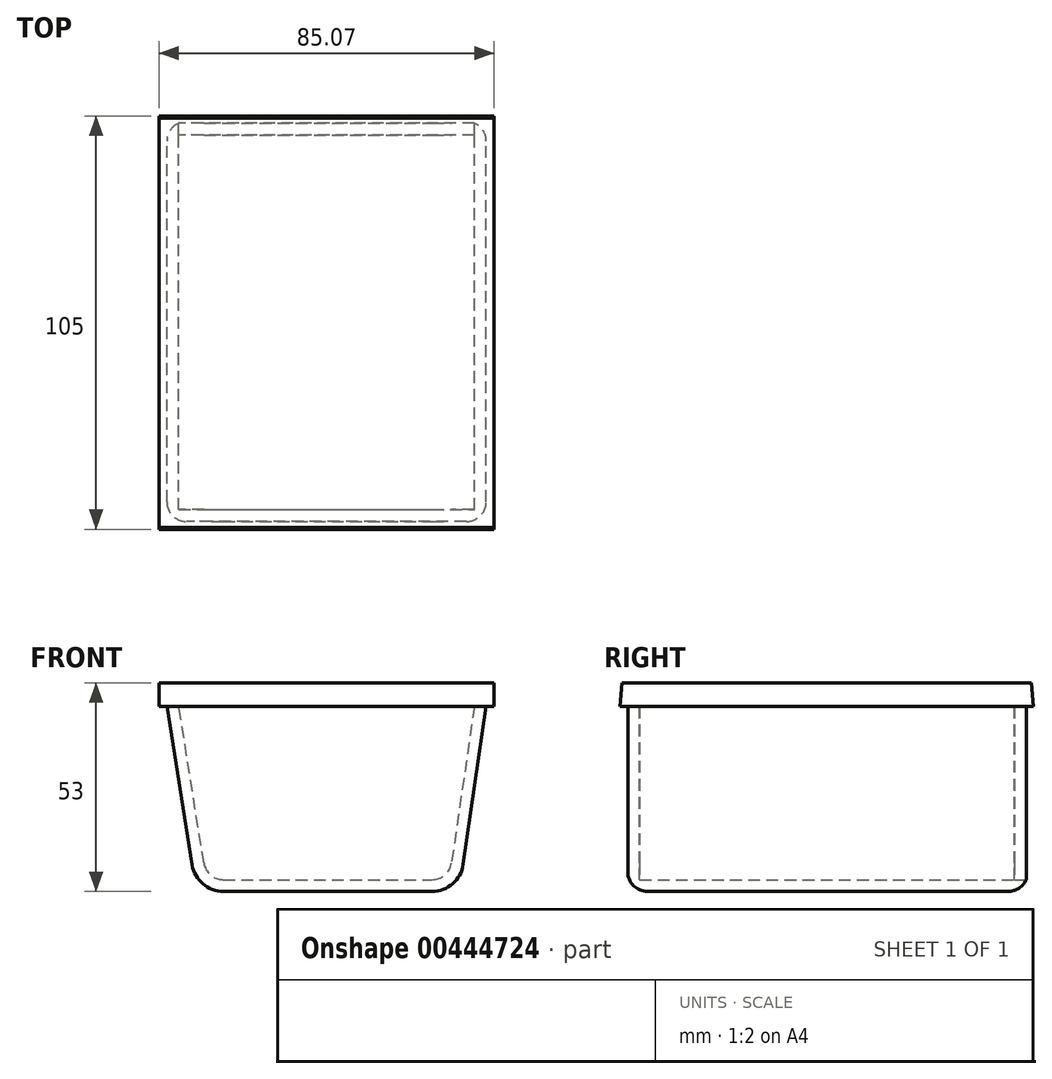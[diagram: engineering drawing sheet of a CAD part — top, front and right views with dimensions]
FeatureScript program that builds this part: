
annotation { "Feature Type Name" : "Feature", "Feature Type Description" : "" }
export const myFeature = defineFeature(function(context is Context, id is Id, definition is map)
    precondition{}
    {
        {
            var Q0;
            Q0=qCreatedBy(makeId("Front.planeOp"),FACE);
            var sketch = newSketch(context, id + "F0", { "sketchPlane" : qUnion([Q0])});
            skLineSegment(sketch, "E0", {"start": v(4.26, 0) * mm, "end": v(57.3, 0) * mm});
            skLineSegment(sketch, "E1", {"start": v(-0.67, 4.21) * mm, "end": v(-7.04, 44) * mm});
            skLineSegment(sketch, "E2", {"start": v(68.03, 44) * mm, "end": v(62.25, 4.28) * mm});
            skPoint(sketch, "E3.start.orphan", {"position": v(30.82, 0) * mm});
            skPoint(sketch, "E4.visualSharp", {"position": v(61.63, 0) * mm});
            skArc(sketch, "E4.filletArc", {"start": v(57.3, 0) * mm, "mid": v(60.58, 1.22) * mm, "end": v(62.25, 4.28) * mm});
            skPoint(sketch, "E5.visualSharp", {"position": v(0, 0) * mm});
            skArc(sketch, "E5.filletArc", {"start": v(-0.67, 4.21) * mm, "mid": v(1.02, 1.2) * mm, "end": v(4.26, 0) * mm});
            skLineSegment(sketch, "E6.1", {"start": v(71.06, 44) * mm, "end": v(65.22, 3.85) * mm});
            skLineSegment(sketch, "E6.2", {"start": v(-3.64, 3.74) * mm, "end": v(-10.08, 44) * mm});
            skArc(sketch, "E6.3", {"start": v(-3.64, 3.74) * mm, "mid": v(-0.93, -1.09) * mm, "end": v(4.26, -3) * mm});
            skLineSegment(sketch, "E6.4", {"start": v(4.26, -3) * mm, "end": v(57.3, -3) * mm});
            skArc(sketch, "E6.6", {"start": v(57.3, -3) * mm, "mid": v(62.54, -1.05) * mm, "end": v(65.22, 3.85) * mm});
            skLineSegment(sketch, "E7", {"start": v(-7.04, 44) * mm, "end": v(-10.08, 44) * mm});
            skLineSegment(sketch, "E8", {"start": v(68.03, 44) * mm, "end": v(71.06, 44) * mm});
            skSolve(sketch);
        }
        {
            var Q0;
            Q0 = qSketchRegion(id + "F0", true);
            extrude(context, id + "F1", {"entities" : qUnion([Q0]), "depth" : 101.22 * mm});
        }
        {
            var Q0;
            Q0=makeQuery(id+"F1.opExtrude","CAP_FACE",FACE,{"disambiguationData":[OSD([sQuery(id+"F0.wireOp",EDGE,"E0"),sQuery(id+"F0.wireOp",EDGE,"E1"),sQuery(id+"F0.wireOp",EDGE,"E2"),sQuery(id+"F0.wireOp",EDGE,"E4.filletArc"),sQuery(id+"F0.wireOp",EDGE,"E5.filletArc"),sQuery(id+"F0.wireOp",EDGE,"E6.1"),sQuery(id+"F0.wireOp",EDGE,"E6.2"),sQuery(id+"F0.wireOp",EDGE,"E6.3"),sQuery(id+"F0.wireOp",EDGE,"E6.4"),sQuery(id+"F0.wireOp",EDGE,"E6.6"),sQuery(id+"F0.wireOp",EDGE,"E7"),sQuery(id+"F0.wireOp",EDGE,"E8")])],"isStart":false});
            var sketch = newSketch(context, id + "F2", { "sketchPlane" : qUnion([Q0])});
            skLineSegment(sketch, "E9", {"start": v(-7.04, 44) * mm, "end": v(68.03, 44) * mm});
            skLineSegment(sketch, "E10.0", {"start": v(-0.67, 4.21) * mm, "end": v(-7.12, 44.47) * mm});
            skLineSegment(sketch, "E10.1", {"start": v(68.1, 44.43) * mm, "end": v(62.25, 4.28) * mm});
            skArc(sketch, "E10.2", {"start": v(57.3, 0) * mm, "mid": v(60.58, 1.22) * mm, "end": v(62.25, 4.28) * mm});
            skLineSegment(sketch, "E10.3", {"start": v(4.26, 0) * mm, "end": v(57.3, 0) * mm});
            skArc(sketch, "E10.4", {"start": v(-0.67, 4.21) * mm, "mid": v(1.02, 1.2) * mm, "end": v(4.26, 0) * mm});
            skSolve(sketch);
        }
        {
            var Q0;
            Q0 = qSketchRegion(id + "F2", true);
            extrude(context, id + "F3", {"entities" : qUnion([Q0]), "operationType" : NewBodyOperationType.ADD, "oppositeDirection" : true, "depth" : 3 * mm});
        }
        {
            var Q0;
            Q0=makeQuery(id+"F1.opExtrude","CAP_FACE",FACE,{"disambiguationData":[OSD([sQuery(id+"F0.wireOp",EDGE,"E0"),sQuery(id+"F0.wireOp",EDGE,"E1"),sQuery(id+"F0.wireOp",EDGE,"E2"),sQuery(id+"F0.wireOp",EDGE,"E4.filletArc"),sQuery(id+"F0.wireOp",EDGE,"E5.filletArc"),sQuery(id+"F0.wireOp",EDGE,"E6.1"),sQuery(id+"F0.wireOp",EDGE,"E6.2"),sQuery(id+"F0.wireOp",EDGE,"E6.3"),sQuery(id+"F0.wireOp",EDGE,"E6.4"),sQuery(id+"F0.wireOp",EDGE,"E6.6"),sQuery(id+"F0.wireOp",EDGE,"E7"),sQuery(id+"F0.wireOp",EDGE,"E8")])],"isStart":true});
            var sketch = newSketch(context, id + "F4", { "sketchPlane" : qUnion([Q0])});
            skLineSegment(sketch, "E11.0", {"start": v(0.67, 4.21) * mm, "end": v(7.04, 44) * mm});
            skArc(sketch, "E11.2", {"start": v(-57.3, 0) * mm, "mid": v(-60.58, 1.22) * mm, "end": v(-62.25, 4.28) * mm});
            skLineSegment(sketch, "E11.3", {"start": v(-4.26, 0) * mm, "end": v(-57.3, 0) * mm});
            skArc(sketch, "E11.4", {"start": v(0.67, 4.21) * mm, "mid": v(-1.02, 1.2) * mm, "end": v(-4.26, 0) * mm});
            skPoint(sketch, "E12", {"position": v(-68.03, 44) * mm});
            skLineSegment(sketch, "E13", {"start": v(-68.03, 44) * mm, "end": v(7.04, 44) * mm});
            skLineSegment(sketch, "E14", {"start": v(-68.03, 44) * mm, "end": v(-62.25, 4.28) * mm});
            skSolve(sketch);
        }
        {
            var Q0;
            Q0 = qSketchRegion(id + "F4", true);
            extrude(context, id + "F5", {"entities" : qUnion([Q0]), "oppositeDirection" : true, "depth" : 3 * mm});
        }
        {
            var Q0;
            Q0=makeQuery(id+"F1.opExtrude","CAP_EDGE",EDGE,{"disambiguationData":[OSD([sQuery(id+"F0.wireOp",EDGE,"E6.1")])],"isStart":true});
            fillet(context, id + "F6", {"entities" : qUnion([Q0]), "radius" : 5 * mm, "tangentPropagation" : true, "allowEdgeOverflow" : false});
        }
        {
            var Q0;
            Q0=makeQuery(id+"F1.opExtrude","CAP_EDGE",EDGE,{"disambiguationData":[OSD([sQuery(id+"F0.wireOp",EDGE,"E6.2")])],"isStart":false});
            fillet(context, id + "F7", {"entities" : qUnion([Q0]), "radius" : 5 * mm, "tangentPropagation" : true, "allowEdgeOverflow" : false});
        }
        {
            var Q0;
            Q0=makeQuery(id+"F3.boolean.opBoolean","MERGE",FACE,{"derivedFrom":[makeQuery(id+"F1.opExtrude","SWEPT_FACE",FACE,{"disambiguationData":[OSD([sQuery(id+"F0.wireOp",EDGE,"E7")])]}),makeQuery(id+"F1.opExtrude","SWEPT_FACE",FACE,{"disambiguationData":[OSD([sQuery(id+"F0.wireOp",EDGE,"E8")])]}),makeQuery(id+"F3.opExtrude","SWEPT_FACE",FACE,{"disambiguationData":[OSD([sQuery(id+"F2.wireOp",EDGE,"E9")])]})]});
            var sketch = newSketch(context, id + "F8", { "sketchPlane" : qUnion([Q0])});
            skLineSegment(sketch, "E15", {"start": v(-12.04, -98.22) * mm, "end": v(-12.04, -103.22) * mm});
            skLineSegment(sketch, "E16", {"start": v(73.03, -98.22) * mm, "end": v(73.03, -103.22) * mm});
            skLineSegment(sketch, "E17", {"start": v(73.03, -103.22) * mm, "end": v(-12.04, -103.22) * mm});
            skLineSegment(sketch, "E18", {"start": v(73.03, -3.22) * mm, "end": v(73.03, -98.22) * mm});
            skLineSegment(sketch, "E19", {"start": v(73.03, -3.22) * mm, "end": v(73.03, 1.78) * mm});
            skLineSegment(sketch, "E20", {"start": v(73.03, 1.78) * mm, "end": v(-12.04, 1.78) * mm});
            skLineSegment(sketch, "E21", {"start": v(-12.04, 1.78) * mm, "end": v(-12.04, -98.22) * mm});
            skPoint(sketch, "E22.end.orphan", {"position": v(68.03, 1.78) * mm});
            skSolve(sketch);
        }
        {
            var Q0;
            Q0 = qSketchRegion(id + "F8", true);
            extrude(context, id + "F9", {"entities" : qUnion([Q0]), "depth" : 6 * mm});
        }
        {
            var Q0;
            Q0=makeQuery(id+"F9.opExtrude","SWEPT_FACE",FACE,{"disambiguationData":[OSD([sQuery(id+"F8.wireOp",EDGE,"E15"),sQuery(id+"F8.wireOp",EDGE,"E21")])]});
            var sketch = newSketch(context, id + "F10", { "sketchPlane" : qUnion([Q0])});
            skLineSegment(sketch, "E23", {"start": v(-1.78, 44) * mm, "end": v(103.22, 44) * mm});
            skLineSegment(sketch, "E24", {"start": v(103.22, 44) * mm, "end": v(103.22, 50) * mm});
            skLineSegment(sketch, "E25", {"start": v(103.22, 44) * mm, "end": v(102.7, 50) * mm});
            skLineSegment(sketch, "E26", {"start": v(-1.78, 44) * mm, "end": v(-1.78, 50) * mm});
            skLineSegment(sketch, "E27", {"start": v(-1.78, 44) * mm, "end": v(-1.26, 50) * mm});
            skLineSegment(sketch, "E28", {"start": v(-1.26, 50) * mm, "end": v(-1.78, 50) * mm});
            skLineSegment(sketch, "E29", {"start": v(103.22, 50) * mm, "end": v(102.7, 50) * mm});
            skSolve(sketch);
        }
        {
            var Q0;
            Q0 = qSketchRegion(id + "F10", true);
            extrude(context, id + "F11", {"entities" : qUnion([Q0]), "operationType" : NewBodyOperationType.REMOVE, "oppositeDirection" : true, "depth" : 111.14 * mm});
        }
    });
